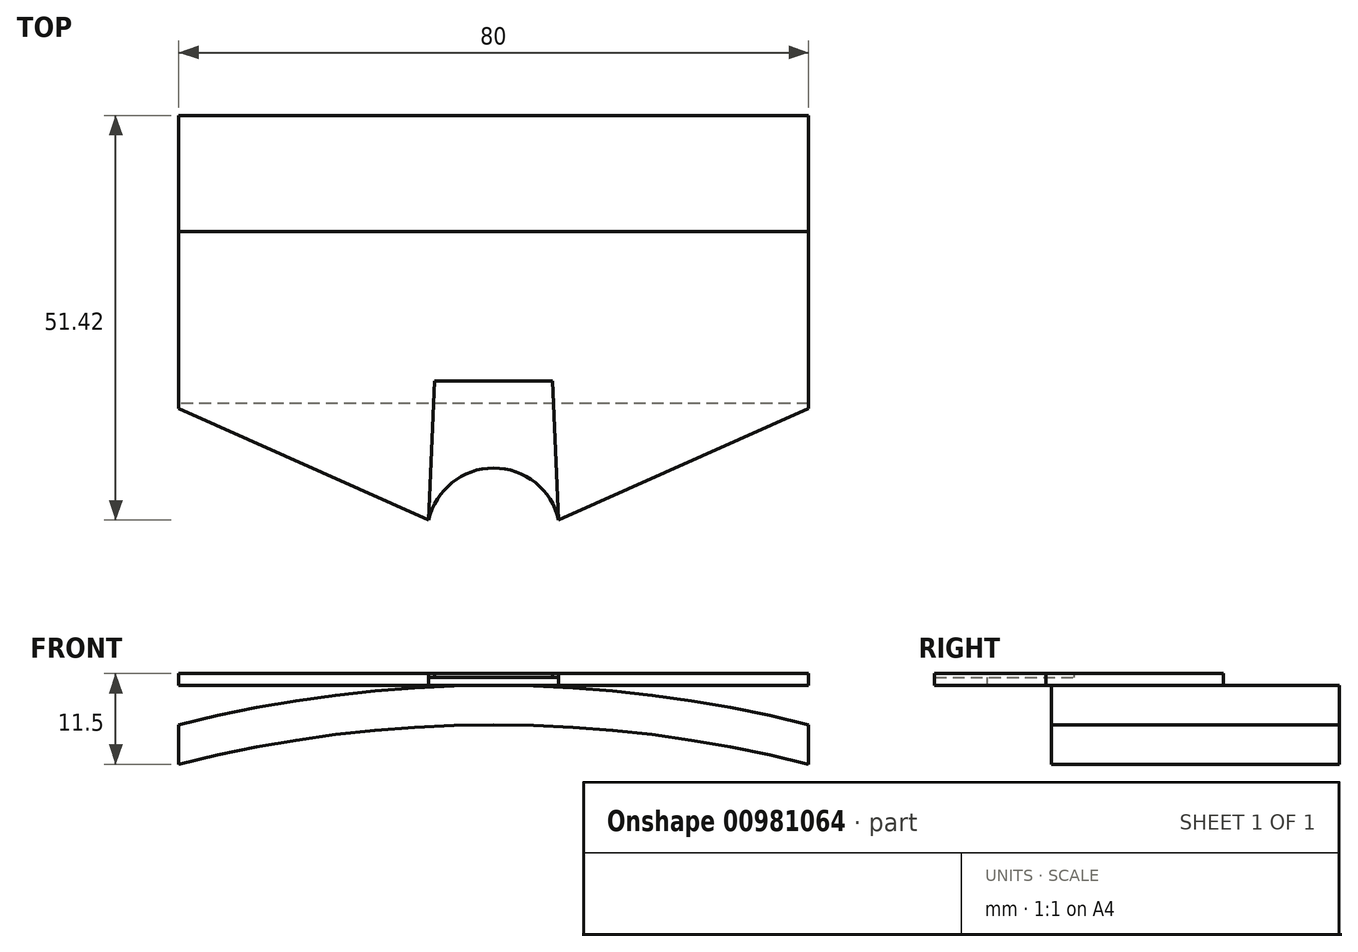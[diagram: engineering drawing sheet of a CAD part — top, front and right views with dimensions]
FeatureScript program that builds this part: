
annotation { "Feature Type Name" : "Feature", "Feature Type Description" : "" }
export const myFeature = defineFeature(function(context is Context, id is Id, definition is map)
    precondition{}
    {
        {
            var Q0;
            Q0=qCreatedBy(makeId("Top.planeOp"),FACE);
            var sketch = newSketch(context, id + "F0", { "sketchPlane" : qUnion([Q0])});
            skLineSegment(sketch, "E0.bottom", {"start": v(-32.75, -16.65) * mm, "end": v(42.25, -16.65) * mm, "construction": true});
            skLineSegment(sketch, "E0.top", {"start": v(-32.75, 19.35) * mm, "end": v(42.25, 19.35) * mm, "construction": true});
            skLineSegment(sketch, "E0.left", {"start": v(-32.75, -16.65) * mm, "end": v(-32.75, 19.35) * mm, "construction": true});
            skLineSegment(sketch, "E0.right", {"start": v(42.25, -16.65) * mm, "end": v(42.25, 19.35) * mm, "construction": true});
            skPoint(sketch, "E1", {"position": v(4.75, -16.65) * mm});
            skCircle(sketch, "E2", {"center": v(4.75, -16.65) * mm, "radius": 8.45 * mm});
            skLineSegment(sketch, "E3", {"start": v(-32.75, 19.35) * mm, "end": v(-32.75, -0.65) * mm, "construction": true});
            skLineSegment(sketch, "E4", {"start": v(-32.75, -0.65) * mm, "end": v(-3.7, -16.65) * mm, "construction": true});
            skLineSegment(sketch, "E5", {"start": v(42.25, 19.35) * mm, "end": v(42.25, -0.65) * mm});
            skLineSegment(sketch, "E6", {"start": v(42.25, -0.65) * mm, "end": v(13.2, -16.65) * mm, "construction": true});
            skLineSegment(sketch, "E7", {"start": v(-3.5, -14.82) * mm, "end": v(13, -14.82) * mm, "construction": true});
            skLineSegment(sketch, "E8", {"start": v(4.75, -16.65) * mm, "end": v(4.75, 2.85) * mm, "construction": true});
            skLineSegment(sketch, "E9", {"start": v(4.75, 2.85) * mm, "end": v(-2.75, 2.85) * mm});
            skLineSegment(sketch, "E10.MirrorCS", {"start": v(4.75, 2.85) * mm, "end": v(12.25, 2.85) * mm});
            skLineSegment(sketch, "E11", {"start": v(-3.5, -14.82) * mm, "end": v(-2.75, 2.85) * mm});
            skLineSegment(sketch, "E12", {"start": v(12.25, 2.85) * mm, "end": v(13, -14.82) * mm});
            skLineSegment(sketch, "E13.0", {"start": v(44.75, 21.85) * mm, "end": v(44.75, -0.65) * mm});
            skLineSegment(sketch, "E13.1", {"start": v(-35.25, 21.85) * mm, "end": v(44.75, 21.85) * mm});
            skLineSegment(sketch, "E13.2", {"start": v(-35.25, 21.85) * mm, "end": v(-35.25, -0.65) * mm});
            skLineSegment(sketch, "E14", {"start": v(-35.25, -0.65) * mm, "end": v(-3.5, -14.82) * mm});
            skLineSegment(sketch, "E15", {"start": v(13, -14.82) * mm, "end": v(44.75, -0.65) * mm});
            skSolve(sketch);
        }
        {
            var Q0;
            Q0=makeQuery(id+"F0.imprint","IMPRINT",FACE,{"disambiguationData":[TD([[makeQuery(id+"F0.imprint","IMPRINT",EDGE,{"derivedFrom":sQuery(id+"F0.wireOp",EDGE,"E9")}),-1.0]])]});
            extrude(context, id + "F1", {"entities" : qUnion([Q0]), "depth" : 1.5 * mm, "offsetDistance" : 25 * mm});
        }
        {
            var Q0;
            Q0=makeQuery(id+"F0.imprint","IMPRINT",FACE,{"disambiguationData":[TD([[makeQuery(id+"F0.imprint","IMPRINT",EDGE,{"derivedFrom":sQuery(id+"F0.wireOp",EDGE,"E9")}),1.0]])]});
            extrude(context, id + "F2", {"entities" : qUnion([Q0]), "operationType" : NewBodyOperationType.ADD, "depth" : 1 * mm, "offsetDistance" : 25 * mm});
        }
        {
            var Q0;
            Q0=qCreatedBy(makeId("Front.planeOp"),FACE);
            var sketch = newSketch(context, id + "F3", { "sketchPlane" : qUnion([Q0])});
            skLineSegment(sketch, "E16.bottom", {"start": v(-35.25, 0) * mm, "end": v(44.75, 0) * mm});
            skLineSegment(sketch, "E16.top", {"start": v(-35.25, -10) * mm, "end": v(44.75, -10) * mm, "construction": true});
            skLineSegment(sketch, "E16.left", {"start": v(44.75, 0) * mm, "end": v(44.75, -10) * mm, "construction": true});
            skLineSegment(sketch, "E16.right", {"start": v(-35.25, 0) * mm, "end": v(-35.25, -10) * mm, "construction": true});
            skPoint(sketch, "E17", {"position": v(4.75, 0) * mm});
            skLineSegment(sketch, "E18", {"start": v(4.75, 0) * mm, "end": v(4.75, -10) * mm, "construction": true});
            skPoint(sketch, "E19", {"position": v(4.75, -5) * mm});
            skArc(sketch, "E20", {"start": v(-35.25, -10) * mm, "mid": v(4.75, -5) * mm, "end": v(44.75, -10) * mm});
            skLineSegment(sketch, "E21", {"start": v(44.75, -10) * mm, "end": v(44.75, -5) * mm});
            skLineSegment(sketch, "E22.MirrorCS", {"start": v(84.75, 0) * mm, "end": v(84.75, -10) * mm, "construction": true});
            skLineSegment(sketch, "E23.MirrorCS", {"start": v(-35.25, -10) * mm, "end": v(-35.25, -5) * mm});
            skArc(sketch, "E24", {"start": v(-35.25, -5) * mm, "mid": v(4.75, 0) * mm, "end": v(44.75, -5) * mm});
            skSolve(sketch);
        }
        {
            var Q0;
            Q0 = qSketchRegion(id + "F3", true);
            extrude(context, id + "F4", {"entities" : qUnion([Q0]), "oppositeDirection" : true, "depth" : 36.6 * mm, "offsetDistance" : 25 * mm});
        }
    });
